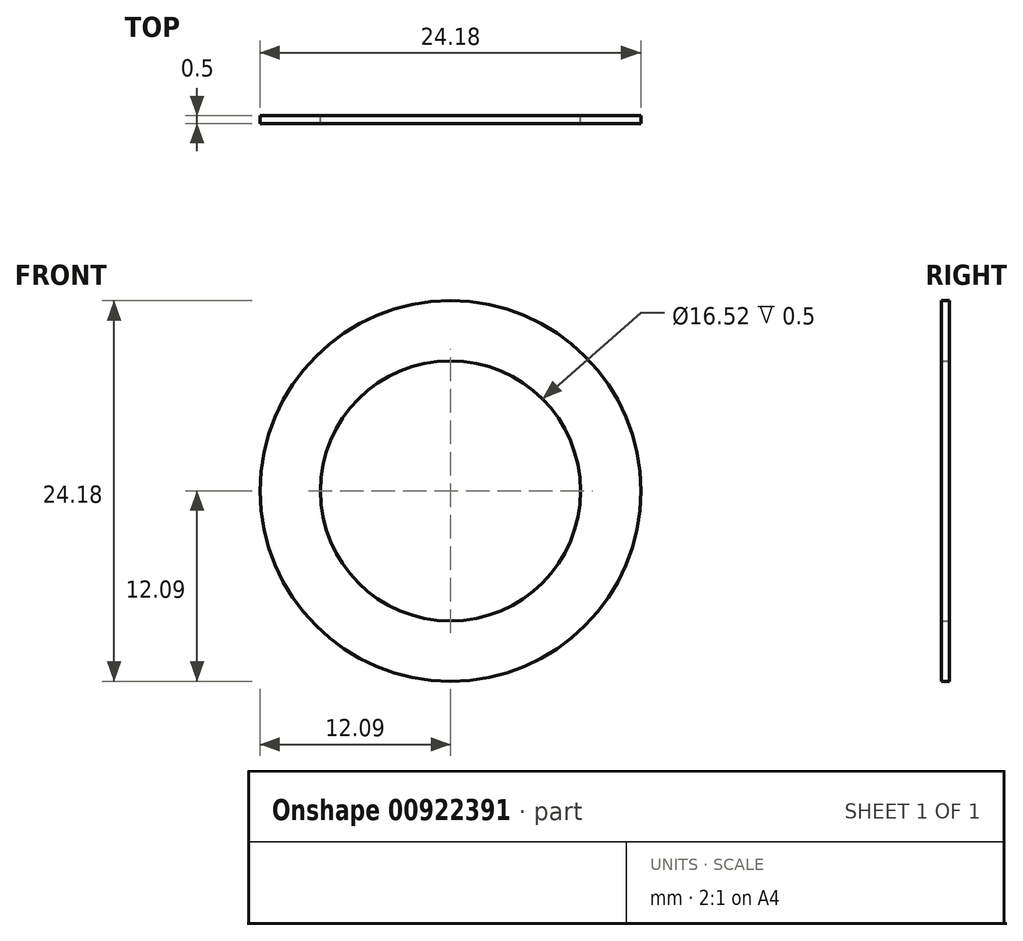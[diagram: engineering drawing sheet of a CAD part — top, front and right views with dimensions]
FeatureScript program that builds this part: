
annotation { "Feature Type Name" : "Feature", "Feature Type Description" : "" }
export const myFeature = defineFeature(function(context is Context, id is Id, definition is map)
    precondition{}
    {
        {
            var Q0;
            Q0=qCreatedBy(makeId("Front.planeOp"),FACE);
            var sketch = newSketch(context, id + "F0", { "sketchPlane" : qUnion([Q0])});
            skCircle(sketch, "E0", {"center": v(0, 0) * mm, "radius": 12.1 * mm});
            skCircle(sketch, "E1", {"center": v(0, 0) * mm, "radius": 8.26 * mm});
            skSolve(sketch);
        }
        {
            var Q0;
            Q0 = qSketchRegion(id + "F0", true);
            extrude(context, id + "F1", {"entities" : qUnion([Q0]), "depth" : 0.5 * mm, "offsetDistance" : 25 * mm});
        }
    });
